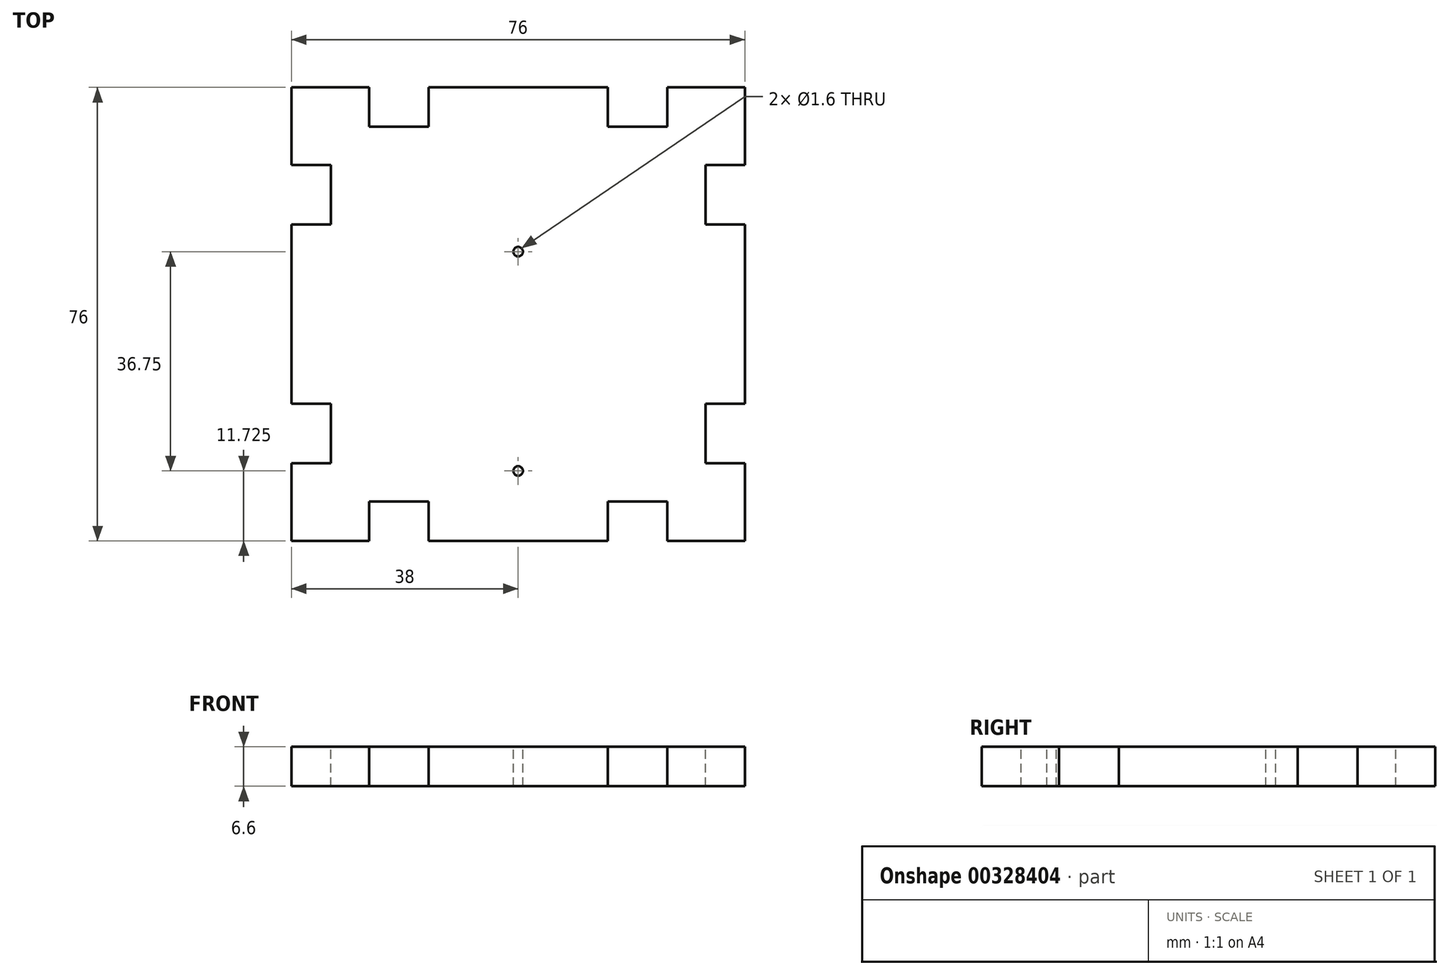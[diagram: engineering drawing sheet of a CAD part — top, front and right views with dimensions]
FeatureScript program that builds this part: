
annotation { "Feature Type Name" : "Feature", "Feature Type Description" : "" }
export const myFeature = defineFeature(function(context is Context, id is Id, definition is map)
    precondition{}
    {
        {
            var Q0;
            Q0=qCreatedBy(makeId("Top.planeOp"),FACE);
            var sketch = newSketch(context, id + "F0", { "sketchPlane" : qUnion([Q0])});
            skLineSegment(sketch, "E0.bottom", {"start": v(38, 38) * mm, "end": v(-38, 38) * mm});
            skLineSegment(sketch, "E0.top", {"start": v(38, -38) * mm, "end": v(-38, -38) * mm});
            skLineSegment(sketch, "E0.left", {"start": v(38, 38) * mm, "end": v(38, -38) * mm});
            skLineSegment(sketch, "E0.right", {"start": v(-38, 38) * mm, "end": v(-38, -38) * mm});
            skLineSegment(sketch, "E1", {"start": v(-38, 13) * mm, "end": v(38, 13) * mm, "construction": true});
            skLineSegment(sketch, "E2", {"start": v(-38, 38) * mm, "end": v(38, -38) * mm, "construction": true});
            skLineSegment(sketch, "E3", {"start": v(-38, -38) * mm, "end": v(38, 38) * mm, "construction": true});
            skPoint(sketch, "E4", {"position": v(0, 0) * mm});
            skSolve(sketch);
        }
        {
            var Q0;
            Q0 = qSketchRegion(id + "F0", true);
            extrude(context, id + "F1", {"entities" : qUnion([Q0]), "oppositeDirection" : true, "depth" : 6.6 * mm});
        }
        {
            var Q0;
            {var subQ0=sQuery(id+"F0.wireOp",EDGE,"E0.top");var subQ1=sQuery(id+"F0.wireOp",EDGE,"E0.right");var subQ2=sQuery(id+"F0.wireOp",EDGE,"E0.bottom");var subQ3=sQuery(id+"F0.wireOp",EDGE,"TOn2y3SU-Vc34-izZE-Xn1k-1RhqRMj2jbJt");var subQ4=sQuery(id+"F0.wireOp",EDGE,"E0.left");Q0=makeQuery(id+"F5kL9iUhUHyoTYB_1.boolean.opBoolean","SPLIT",FACE,{"disambiguationData":[TD([makeQuery(id+"F1.opExtrude","SWEPT_FACE",FACE,{"disambiguationData":[OSD([subQ2])]})])],"derivedFrom":makeQuery(id+"F1.opExtrude","CAP_FACE",FACE,{"disambiguationData":[OSD([subQ2,subQ0,subQ4,subQ1,subQ3])],"isStart":true})});}
            var sketch = newSketch(context, id + "F2", { "sketchPlane" : qUnion([Q0])});
            skLineSegment(sketch, "E5", {"start": v(0, 38) * mm, "end": v(0, -38) * mm, "construction": true});
            skLineSegment(sketch, "E6", {"start": v(-38, 0) * mm, "end": v(38, 0) * mm, "construction": true});
            skLineSegment(sketch, "E7.bottom", {"start": v(15, 38) * mm, "end": v(25, 38) * mm});
            skLineSegment(sketch, "E7.top", {"start": v(15, 31.4) * mm, "end": v(25, 31.4) * mm});
            skLineSegment(sketch, "E7.left", {"start": v(15, 38) * mm, "end": v(15, 31.4) * mm});
            skLineSegment(sketch, "E7.right", {"start": v(25, 38) * mm, "end": v(25, 31.4) * mm});
            skLineSegment(sketch, "E8.MirrorCS", {"start": v(-25, 38) * mm, "end": v(-25, 31.4) * mm});
            skLineSegment(sketch, "E9.MirrorCS", {"start": v(-15, 31.4) * mm, "end": v(-25, 31.4) * mm});
            skLineSegment(sketch, "E10.MirrorCS", {"start": v(-15, 38) * mm, "end": v(-15, 31.4) * mm});
            skLineSegment(sketch, "E11.MirrorCS", {"start": v(-15, 38) * mm, "end": v(-25, 38) * mm});
            skLineSegment(sketch, "E12.1.0", {"start": v(-38, -25) * mm, "end": v(-31.4, -25) * mm});
            skLineSegment(sketch, "E12.1.1", {"start": v(-31.4, 15) * mm, "end": v(-31.4, 25) * mm});
            skLineSegment(sketch, "E12.1.2", {"start": v(-38, -15) * mm, "end": v(-31.4, -15) * mm});
            skLineSegment(sketch, "E12.1.3", {"start": v(-38, 25) * mm, "end": v(-31.4, 25) * mm});
            skLineSegment(sketch, "E12.1.4", {"start": v(-38, 15) * mm, "end": v(-31.4, 15) * mm});
            skLineSegment(sketch, "E12.1.5", {"start": v(-38, 15) * mm, "end": v(-38, 25) * mm});
            skLineSegment(sketch, "E12.1.6", {"start": v(-31.4, -15) * mm, "end": v(-31.4, -25) * mm});
            skLineSegment(sketch, "E12.1.7", {"start": v(-38, -15) * mm, "end": v(-38, -25) * mm});
            skLineSegment(sketch, "E12.2.0", {"start": v(25, -38) * mm, "end": v(25, -31.4) * mm});
            skLineSegment(sketch, "E12.2.1", {"start": v(-15, -31.4) * mm, "end": v(-25, -31.4) * mm});
            skLineSegment(sketch, "E12.2.2", {"start": v(15, -38) * mm, "end": v(15, -31.4) * mm});
            skLineSegment(sketch, "E12.2.3", {"start": v(-25, -38) * mm, "end": v(-25, -31.4) * mm});
            skLineSegment(sketch, "E12.2.4", {"start": v(-15, -38) * mm, "end": v(-15, -31.4) * mm});
            skLineSegment(sketch, "E12.2.5", {"start": v(-15, -38) * mm, "end": v(-25, -38) * mm});
            skLineSegment(sketch, "E12.2.6", {"start": v(15, -31.4) * mm, "end": v(25, -31.4) * mm});
            skLineSegment(sketch, "E12.2.7", {"start": v(15, -38) * mm, "end": v(25, -38) * mm});
            skLineSegment(sketch, "E12.3.0", {"start": v(38, 25) * mm, "end": v(31.4, 25) * mm});
            skLineSegment(sketch, "E12.3.1", {"start": v(31.4, -15) * mm, "end": v(31.4, -25) * mm});
            skLineSegment(sketch, "E12.3.2", {"start": v(38, 15) * mm, "end": v(31.4, 15) * mm});
            skLineSegment(sketch, "E12.3.3", {"start": v(38, -25) * mm, "end": v(31.4, -25) * mm});
            skLineSegment(sketch, "E12.3.4", {"start": v(38, -15) * mm, "end": v(31.4, -15) * mm});
            skLineSegment(sketch, "E12.3.5", {"start": v(38, -15) * mm, "end": v(38, -25) * mm});
            skLineSegment(sketch, "E12.3.6", {"start": v(31.4, 15) * mm, "end": v(31.4, 25) * mm});
            skLineSegment(sketch, "E12.3.7", {"start": v(38, 15) * mm, "end": v(38, 25) * mm});
            skPoint(sketch, "E12.center", {"position": v(0, 0) * mm});
            skSolve(sketch);
        }
        {
            var Q0;
            Q0 = qSketchRegion(id + "F2", true);
            extrude(context, id + "F3", {"entities" : qUnion([Q0]), "operationType" : NewBodyOperationType.REMOVE, "endBound" : BoundingType.UP_TO_NEXT, "oppositeDirection" : true, "depth" : 25 * mm});
        }
        {
            var Q0;
            Q0=makeQuery(id+"F1.opExtrude","CAP_FACE",FACE,{"disambiguationData":[OSD([sQuery(id+"F0.wireOp",EDGE,"E0.bottom"),sQuery(id+"F0.wireOp",EDGE,"E0.top"),sQuery(id+"F0.wireOp",EDGE,"E0.left"),sQuery(id+"F0.wireOp",EDGE,"E0.right")])],"isStart":true});
            var sketch = newSketch(context, id + "F4", { "sketchPlane" : qUnion([Q0])});
            skLineSegment(sketch, "E13", {"start": v(0, 38) * mm, "end": v(0, -38) * mm, "construction": true});
            skLineSegment(sketch, "E14.bottom", {"start": v(17.5, 15.6) * mm, "end": v(-17.5, 15.6) * mm, "construction": true});
            skLineSegment(sketch, "E14.top", {"start": v(17.5, -31.4) * mm, "end": v(-17.5, -31.4) * mm, "construction": true});
            skLineSegment(sketch, "E14.left", {"start": v(17.5, 15.6) * mm, "end": v(17.5, -31.4) * mm, "construction": true});
            skLineSegment(sketch, "E14.right", {"start": v(-17.5, 15.6) * mm, "end": v(-17.5, -31.4) * mm, "construction": true});
            skPoint(sketch, "E14.middle", {"position": v(0, -7.9) * mm});
            skCircle(sketch, "E15", {"center": v(0, 10.48) * mm, "radius": 0.8 * mm});
            skLineSegment(sketch, "E16", {"start": v(-17.5, -7.9) * mm, "end": v(17.5, -7.9) * mm, "construction": true});
            skCircle(sketch, "E17.MirrorC", {"center": v(0, -26.27) * mm, "radius": 0.8 * mm});
            skSolve(sketch);
        }
        {
            var Q0;
            Q0 = qSketchRegion(id + "F4", true);
            extrude(context, id + "F5", {"entities" : qUnion([Q0]), "operationType" : NewBodyOperationType.REMOVE, "endBound" : BoundingType.UP_TO_NEXT, "oppositeDirection" : true, "depth" : 6 * mm});
        }
    });
